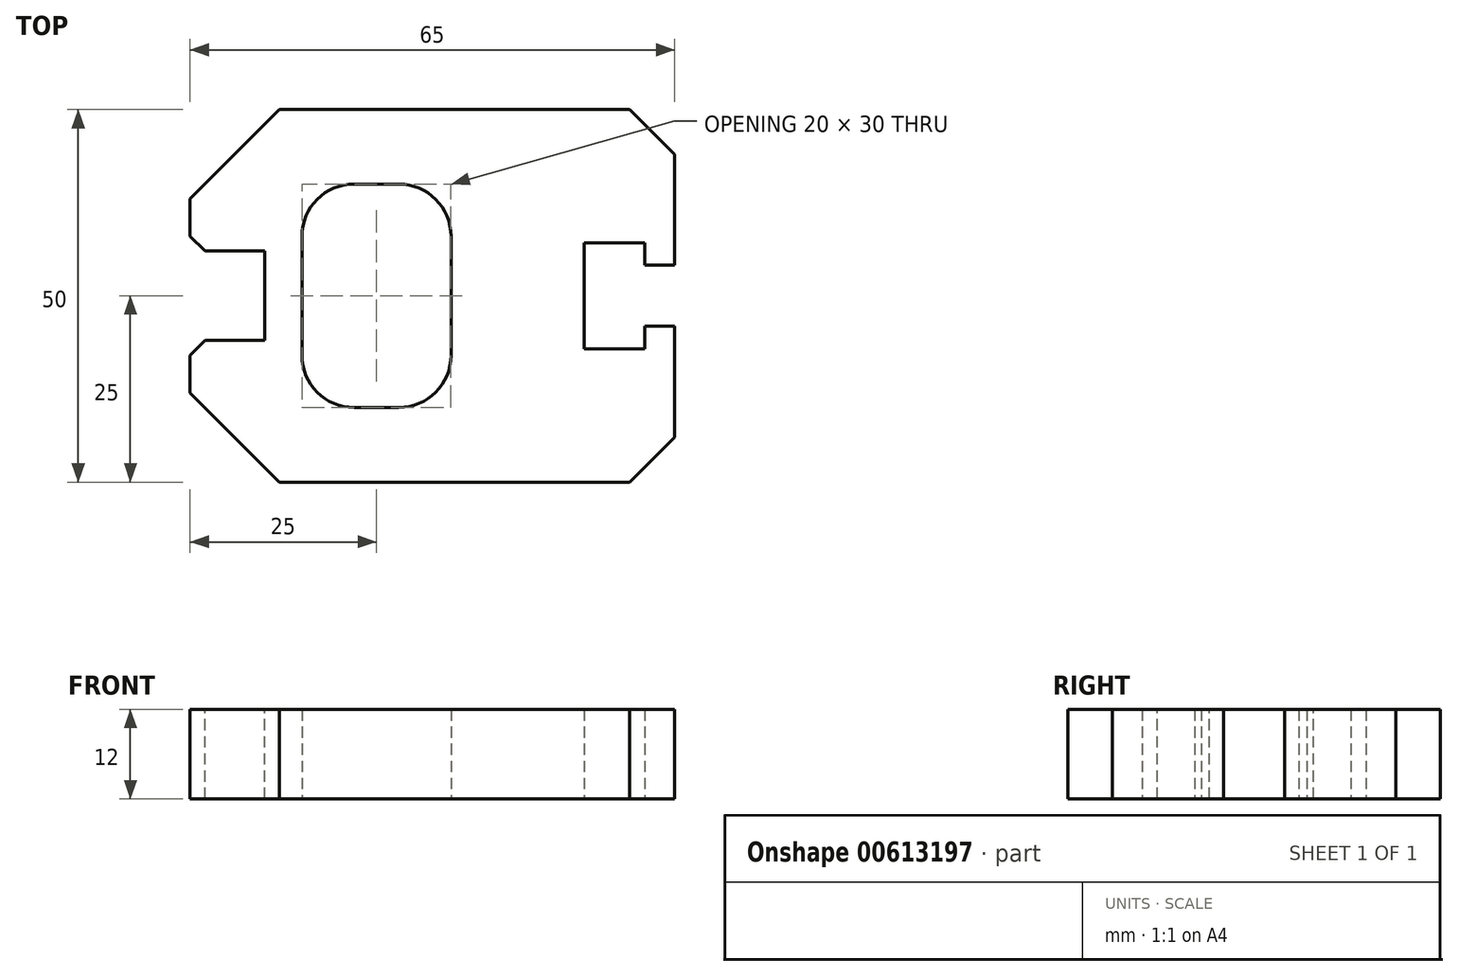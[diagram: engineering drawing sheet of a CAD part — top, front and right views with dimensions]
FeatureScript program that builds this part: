
annotation { "Feature Type Name" : "Feature", "Feature Type Description" : "" }
export const myFeature = defineFeature(function(context is Context, id is Id, definition is map)
    precondition{}
    {
        {
            var Q0;
            Q0=qCreatedBy(makeId("Top.planeOp"),FACE);
            var sketch = newSketch(context, id + "F0", { "sketchPlane" : qUnion([Q0])});
            skLineSegment(sketch, "E0.bottom", {"start": v(-40, 25) * mm, "end": v(40, 25) * mm});
            skLineSegment(sketch, "E0.top", {"start": v(-40, -25) * mm, "end": v(40, -25) * mm});
            skLineSegment(sketch, "E0.left", {"start": v(-40, 25) * mm, "end": v(-40, -25) * mm});
            skLineSegment(sketch, "E0.right", {"start": v(40, 25) * mm, "end": v(40, 4.1) * mm});
            skPoint(sketch, "E0.middle", {"position": v(0, 0) * mm});
            skLineSegment(sketch, "E1.bottom", {"start": v(36, 4.1) * mm, "end": v(40, 4.1) * mm});
            skLineSegment(sketch, "E1.top", {"start": v(36, -4.1) * mm, "end": v(40, -4.1) * mm});
            skPoint(sketch, "E1.middle", {"position": v(40, 0) * mm});
            skLineSegment(sketch, "E2", {"start": v(36, -4.1) * mm, "end": v(36, -7.1) * mm});
            skLineSegment(sketch, "E3", {"start": v(36, -7.1) * mm, "end": v(27.9, -7.1) * mm});
            skLineSegment(sketch, "E4", {"start": v(27.9, 7.1) * mm, "end": v(36, 7.1) * mm});
            skLineSegment(sketch, "E5", {"start": v(36, 7.1) * mm, "end": v(36, 4.1) * mm});
            skLineSegment(sketch, "E6.trimOffspring", {"start": v(40, -4.1) * mm, "end": v(40, -25) * mm});
            skPoint(sketch, "E1.right.end.orphan", {"position": v(44, -4.1) * mm});
            skPoint(sketch, "E7.orphan", {"position": v(44, 4.1) * mm});
            skLineSegment(sketch, "E8", {"start": v(27.9, -7.1) * mm, "end": v(27.9, 7.1) * mm});
            skSolve(sketch);
        }
        {
            var Q0;
            Q0 = qSketchRegion(id + "F0", true);
            extrude(context, id + "F1", {"entities" : qUnion([Q0]), "depth" : 12 * mm, "offsetDistance" : 25 * mm});
        }
        {
            var Q0;
            Q0=makeQuery(id+"F1.opExtrude","SWEPT_FACE",FACE,{"disambiguationData":[OSD([sQuery(id+"F0.wireOp",EDGE,"E0.left")])]});
            var sketch = newSketch(context, id + "F2", { "sketchPlane" : qUnion([Q0])});
            skLineSegment(sketch, "E9.bottom", {"start": v(6, -28.6) * mm, "end": v(-6, -28.6) * mm});
            skLineSegment(sketch, "E9.top", {"start": v(6, 52.6) * mm, "end": v(-6, 52.6) * mm});
            skLineSegment(sketch, "E9.left", {"start": v(6, -28.6) * mm, "end": v(6, 52.6) * mm});
            skLineSegment(sketch, "E9.right", {"start": v(-6, -28.6) * mm, "end": v(-6, 52.6) * mm});
            skPoint(sketch, "E9.middle", {"position": v(0, 12) * mm});
            skSolve(sketch);
        }
        {
            var Q0;
            {var subQ0=sQuery(id+"F2.wireOp",EDGE,"E9.left");var subQ1=sQuery(id+"F0.wireOp",EDGE,"E0.left");var subQ2=makeQuery(id+"F1.opExtrude","CAP_EDGE",EDGE,{"disambiguationData":[OSD([subQ1])],"isStart":true});var subQ3=makeQuery(id+"F2.imprint","INTERSECT",VERTEX,{"derivedFrom":[subQ2,subQ0]});Q0=makeQuery(id+"F2.imprint","IMPRINT",FACE,{"disambiguationData":[TD([[makeQuery(id+"F2.imprint","IMPRINT",EDGE,{"disambiguationData":[TD([[subQ3,-1.0]])],"derivedFrom":subQ0}),1.0]])]});}
            extrude(context, id + "F3", {"entities" : qUnion([Q0]), "operationType" : NewBodyOperationType.REMOVE, "oppositeDirection" : true, "depth" : 25 * mm, "offsetDistance" : 25 * mm});
        }
        {
            var Q0;
            Q0=makeQuery(id+"F1.opExtrude","SWEPT_EDGE",EDGE,{"disambiguationData":[OSD([sQuery(id+"F0.wireOp",EDGE,"E0.top"),sQuery(id+"F0.wireOp",EDGE,"E0.left")])]});
            var Q1;
            Q1=makeQuery(id+"F1.opExtrude","SWEPT_EDGE",EDGE,{"disambiguationData":[OSD([sQuery(id+"F0.wireOp",EDGE,"E0.bottom"),sQuery(id+"F0.wireOp",EDGE,"E0.left")])]});
            var Q2;
            Q2=makeQuery(id+"F3.boolean.opBoolean","COPY",EDGE,{"derivedFrom":makeQuery(id+"F3.opExtrude","CAP_EDGE",EDGE,{"disambiguationData":[OSD([sQuery(id+"F2.wireOp",EDGE,"E9.right")])],"isStart":true})});
            var Q3;
            Q3=makeQuery(id+"F3.boolean.opBoolean","COPY",EDGE,{"derivedFrom":makeQuery(id+"F3.opExtrude","CAP_EDGE",EDGE,{"disambiguationData":[OSD([sQuery(id+"F2.wireOp",EDGE,"E9.left")])],"isStart":true})});
            var Q4;
            Q4=makeQuery(id+"F1.opExtrude","SWEPT_EDGE",EDGE,{"disambiguationData":[OSD([sQuery(id+"F0.wireOp",EDGE,"E0.top"),sQuery(id+"F0.wireOp",EDGE,"E6.trimOffspring")])]});
            var Q5;
            Q5=makeQuery(id+"F1.opExtrude","SWEPT_EDGE",EDGE,{"disambiguationData":[OSD([sQuery(id+"F0.wireOp",EDGE,"E0.bottom"),sQuery(id+"F0.wireOp",EDGE,"E0.right")])]});
            chamfer(context, id + "F4", {"entities" : qUnion([Q0, Q1, Q2, Q3, Q4, Q5]), "width" : 6 * mm, "tangentPropagation" : true});
        }
        {
            var Q0;
            Q0=makeQuery(id+"F1.opExtrude","CAP_FACE",FACE,{"disambiguationData":[OSD([sQuery(id+"F0.wireOp",EDGE,"E0.bottom"),sQuery(id+"F0.wireOp",EDGE,"E0.top"),sQuery(id+"F0.wireOp",EDGE,"E0.left"),sQuery(id+"F0.wireOp",EDGE,"E0.right"),sQuery(id+"F0.wireOp",EDGE,"E1.bottom"),sQuery(id+"F0.wireOp",EDGE,"E1.top"),sQuery(id+"F0.wireOp",EDGE,"E2"),sQuery(id+"F0.wireOp",EDGE,"E3"),sQuery(id+"F0.wireOp",EDGE,"3L8CT1Rc-yPBJ-LkoM-DI7L-FsST9B0KI1JH"),sQuery(id+"F0.wireOp",EDGE,"WNVqmnMc-RUqn-Qs9u-y7ip-Q7h098QSEoGO"),sQuery(id+"F0.wireOp",EDGE,"Pi7qMuu4-cJzI-tp3V-uIzp-7zE57pCL9TCs"),sQuery(id+"F0.wireOp",EDGE,"E4"),sQuery(id+"F0.wireOp",EDGE,"E5"),sQuery(id+"F0.wireOp",EDGE,"E6.trimOffspring")])],"isStart":true});
            var sketch = newSketch(context, id + "F5", { "sketchPlane" : qUnion([Q0])});
            skLineSegment(sketch, "E10.bottom", {"start": v(10, 15) * mm, "end": v(-10, 15) * mm});
            skLineSegment(sketch, "E10.top", {"start": v(10, -15) * mm, "end": v(-10, -15) * mm});
            skLineSegment(sketch, "E10.left", {"start": v(10, 15) * mm, "end": v(10, -15) * mm});
            skLineSegment(sketch, "E10.right", {"start": v(-10, 15) * mm, "end": v(-10, -15) * mm});
            skPoint(sketch, "E10.middle", {"position": v(0, 0) * mm});
            skSolve(sketch);
        }
        {
            var Q0;
            Q0=makeQuery(id+"F5.imprint","IMPRINT",FACE,{"disambiguationData":[TD([[makeQuery(id+"F5.imprint","IMPRINT",EDGE,{"derivedFrom":sQuery(id+"F5.wireOp",EDGE,"E10.bottom")}),1.0]])]});
            extrude(context, id + "F6", {"entities" : qUnion([Q0]), "operationType" : NewBodyOperationType.REMOVE, "oppositeDirection" : true, "depth" : 30 * mm, "offsetDistance" : 25 * mm});
        }
        {
            var Q0;
            Q0=makeQuery(id+"F6.boolean.opBoolean","COPY",EDGE,{"derivedFrom":makeQuery(id+"F6.opExtrude","SWEPT_EDGE",EDGE,{"disambiguationData":[OSD([sQuery(id+"F5.wireOp",EDGE,"E10.top"),sQuery(id+"F5.wireOp",EDGE,"E10.left")])]})});
            var Q1;
            Q1=makeQuery(id+"F6.boolean.opBoolean","COPY",EDGE,{"derivedFrom":makeQuery(id+"F6.opExtrude","SWEPT_EDGE",EDGE,{"disambiguationData":[OSD([sQuery(id+"F5.wireOp",EDGE,"E10.top"),sQuery(id+"F5.wireOp",EDGE,"E10.right")])]})});
            var Q2;
            Q2=makeQuery(id+"F6.boolean.opBoolean","COPY",EDGE,{"derivedFrom":makeQuery(id+"F6.opExtrude","SWEPT_EDGE",EDGE,{"disambiguationData":[OSD([sQuery(id+"F5.wireOp",EDGE,"E10.bottom"),sQuery(id+"F5.wireOp",EDGE,"E10.right")])]})});
            var Q3;
            Q3=makeQuery(id+"F6.boolean.opBoolean","COPY",EDGE,{"derivedFrom":makeQuery(id+"F6.opExtrude","SWEPT_EDGE",EDGE,{"disambiguationData":[OSD([sQuery(id+"F5.wireOp",EDGE,"E10.bottom"),sQuery(id+"F5.wireOp",EDGE,"E10.left")])]})});
            fillet(context, id + "F7", {"entities" : qUnion([Q0, Q1, Q2, Q3]), "radius" : 7 * mm, "tangentPropagation" : true, "allowEdgeOverflow" : false});
        }
        {
            var Q0;
            Q0=makeQuery(id+"F1.opExtrude","CAP_FACE",FACE,{"disambiguationData":[OSD([sQuery(id+"F0.wireOp",EDGE,"E0.bottom"),sQuery(id+"F0.wireOp",EDGE,"E0.top"),sQuery(id+"F0.wireOp",EDGE,"E0.left"),sQuery(id+"F0.wireOp",EDGE,"E0.right"),sQuery(id+"F0.wireOp",EDGE,"E1.bottom"),sQuery(id+"F0.wireOp",EDGE,"E1.top"),sQuery(id+"F0.wireOp",EDGE,"E2"),sQuery(id+"F0.wireOp",EDGE,"E3"),sQuery(id+"F0.wireOp",EDGE,"E4"),sQuery(id+"F0.wireOp",EDGE,"E5"),sQuery(id+"F0.wireOp",EDGE,"E6.trimOffspring"),sQuery(id+"F0.wireOp",EDGE,"E8")])],"isStart":true});
            var sketch = newSketch(context, id + "F8", { "sketchPlane" : qUnion([Q0])});
            skLineSegment(sketch, "E11.bottom", {"start": v(-25, -28.1) * mm, "end": v(-42, -28.1) * mm});
            skLineSegment(sketch, "E11.top", {"start": v(-25, 27.38) * mm, "end": v(-42, 27.38) * mm});
            skLineSegment(sketch, "E11.left", {"start": v(-25, -28.1) * mm, "end": v(-25, 27.38) * mm});
            skLineSegment(sketch, "E11.right", {"start": v(-42, -28.1) * mm, "end": v(-42, 27.38) * mm});
            skSolve(sketch);
        }
        {
            var Q0;
            {var subQ20=sQuery(id+"F8.wireOp",EDGE,"E11.bottom");Q0=makeQuery(id+"F8.imprint","IMPRINT",FACE,{"disambiguationData":[TD([[makeQuery(id+"F8.imprint","IMPRINT",EDGE,{"derivedFrom":subQ20}),-1.0]])]});}
            var Q1;
            {var subQ1=sQuery(id+"F0.wireOp",EDGE,"E0.bottom");var subQ8=sQuery(id+"F8.wireOp",EDGE,"E11.left");var subQ9=makeQuery(id+"F1.opExtrude","CAP_EDGE",EDGE,{"disambiguationData":[OSD([subQ1])],"isStart":true});var subQ10=makeQuery(id+"F8.imprint","INTERSECT",VERTEX,{"derivedFrom":[subQ9,subQ8]});Q1=makeQuery(id+"F8.imprint","IMPRINT",FACE,{"disambiguationData":[TD([[makeQuery(id+"F8.imprint","IMPRINT",EDGE,{"disambiguationData":[TD([[subQ10,-1.0]])],"derivedFrom":subQ8}),1.0]])]});}
            var Q2;
            {var subQ1=sQuery(id+"F0.wireOp",EDGE,"E0.top");var subQ8=sQuery(id+"F8.wireOp",EDGE,"E11.left");var subQ9=makeQuery(id+"F1.opExtrude","CAP_EDGE",EDGE,{"disambiguationData":[OSD([subQ1])],"isStart":true});var subQ10=makeQuery(id+"F8.imprint","INTERSECT",VERTEX,{"derivedFrom":[subQ9,subQ8]});Q2=makeQuery(id+"F8.imprint","IMPRINT",FACE,{"disambiguationData":[TD([[makeQuery(id+"F8.imprint","IMPRINT",EDGE,{"disambiguationData":[TD([[subQ10,1.0]])],"derivedFrom":subQ8}),1.0]])]});}
            extrude(context, id + "F9", {"entities" : qUnion([Q0, Q1, Q2]), "operationType" : NewBodyOperationType.REMOVE, "oppositeDirection" : true, "depth" : 25 * mm, "offsetDistance" : 25 * mm});
        }
        {
            var Q0;
            Q0=makeQuery(id+"F9.boolean.opBoolean","INTERSECT",EDGE,{"derivedFrom":[makeQuery(id+"F1.opExtrude","SWEPT_FACE",FACE,{"disambiguationData":[OSD([sQuery(id+"F0.wireOp",EDGE,"E0.bottom")])]}),makeQuery(id+"F9.opExtrude","SWEPT_FACE",FACE,{"disambiguationData":[OSD([sQuery(id+"F8.wireOp",EDGE,"E11.left")])]})]});
            var Q1;
            Q1=makeQuery(id+"F9.boolean.opBoolean","INTERSECT",EDGE,{"derivedFrom":[makeQuery(id+"F1.opExtrude","SWEPT_FACE",FACE,{"disambiguationData":[OSD([sQuery(id+"F0.wireOp",EDGE,"E0.top")])]}),makeQuery(id+"F9.opExtrude","SWEPT_FACE",FACE,{"disambiguationData":[OSD([sQuery(id+"F8.wireOp",EDGE,"E11.left")])]})]});
            chamfer(context, id + "F10", {"entities" : qUnion([Q0, Q1]), "width" : 12 * mm, "tangentPropagation" : true});
        }
        {
            var Q0;
            Q0=makeQuery(id+"F9.boolean.opBoolean","INTERSECT",EDGE,{"derivedFrom":[makeQuery(id+"F3.boolean.opBoolean","COPY",FACE,{"derivedFrom":makeQuery(id+"F3.opExtrude","SWEPT_FACE",FACE,{"disambiguationData":[OSD([sQuery(id+"F2.wireOp",EDGE,"E9.right")])]})}),makeQuery(id+"F9.opExtrude","SWEPT_FACE",FACE,{"disambiguationData":[OSD([sQuery(id+"F8.wireOp",EDGE,"E11.left")])]})]});
            var Q1;
            Q1=makeQuery(id+"F9.boolean.opBoolean","INTERSECT",EDGE,{"derivedFrom":[makeQuery(id+"F3.boolean.opBoolean","COPY",FACE,{"derivedFrom":makeQuery(id+"F3.opExtrude","SWEPT_FACE",FACE,{"disambiguationData":[OSD([sQuery(id+"F2.wireOp",EDGE,"E9.left")])]})}),makeQuery(id+"F9.opExtrude","SWEPT_FACE",FACE,{"disambiguationData":[OSD([sQuery(id+"F8.wireOp",EDGE,"E11.left")])]})]});
            chamfer(context, id + "F11", {"entities" : qUnion([Q0, Q1]), "width" : 2 * mm, "tangentPropagation" : true});
        }
    });
